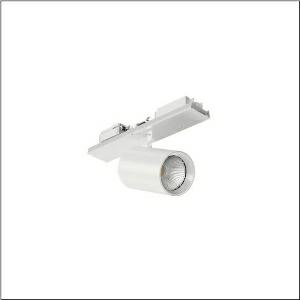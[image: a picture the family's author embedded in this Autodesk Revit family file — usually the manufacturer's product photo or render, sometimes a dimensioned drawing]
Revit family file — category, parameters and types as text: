
# Revit family: licross_spot_31_51sl13da45b
name_source: partatom
category: Lighting Fixtures
units: mm (PartAtom-declared; Revit-internal decimal feet)

## family parameters
Cut with Voids When Loaded = No
Host = Face
Light Source = No
Part Type = Normal
Room Calculation Point = No
Round Connector Dimension = Use Diameter
Shared = No

## types (1)
- --- (1 x LED, 5190 lm, 43.9 W, 4000K)
    Apparent Load = 44 VA
    CIE Flux Codes = 92 97 99 100 100
    Color Rendering = 90
    Color Temperature = 4000K
    Default Elevation = 1800 mm
    Description = Licross Spot 31, directional spotlight, light control with lens, of plastic, LED rated luminous flux: 5.190lm, light colour: 940, with plug, 5-pole, mains connection: 220..240V, AC, 50/60Hz, of aluminium, traffic white (RAL 9016), length: 300mm, diameter: 90mm, protection rating (complete): IP20, insulation class (complete): insulation class I (protective earthing), certification: CE, packaging unit: 1 piece
    Height = 175 mm
    Lamp = 1 x LED
    Lamp Light Flux = 5190 lm
    Lamp Power = 43.9 W
    Lamp count = 1
    Length = 90 mm
    Luminous efficacy = 118 lm/W
    Manufacturer = Siteco
    ModVariant = No
    Model = 51SL13DA45B
    Mounting Place = Ceiling
    Mounting Type = Pendant
    Number of Poles = 1
    OnlyDefault = Yes
    Power Factor = 1
    Product Name = Licross Spot 31
    Product group = directional spotlight
    ProductGroupID = 905
    Protection Class = Protection class I
    Protection Degree = IP 20
    RLX_Detail_Level = 1
    RLX_Emergency_Light_Flux = 0 lm
    RLX_Emergency_Type = 0
    RLX_Emergency_Type_DB = No
    RlxData = <blob elided: 14773 chars, md5=35783ecb>
    Socket = socket
    Standby Power = 0 W
    System Light Flux = 5190 lm
    System Power = 44 W
    Type Comments = factory setting: luminous flux: 100 % | (ON | ON | ON) | 1050 mA
    Type Image = l_1245720.jpg
    URL = http://relux.com
    VarID = @adj_131673
    Voltage = 0 V
    Weight = 0.00 kg
    Width = 0 mm  [stored 0 ft]

note: [stored X ft] marks values corroborated as IEEE doubles in the binary element streams (Revit-internal decimal feet)

## geometry (parser evidence)
native form markers: Sweep x12
no freeform markers — native parametric forms only
